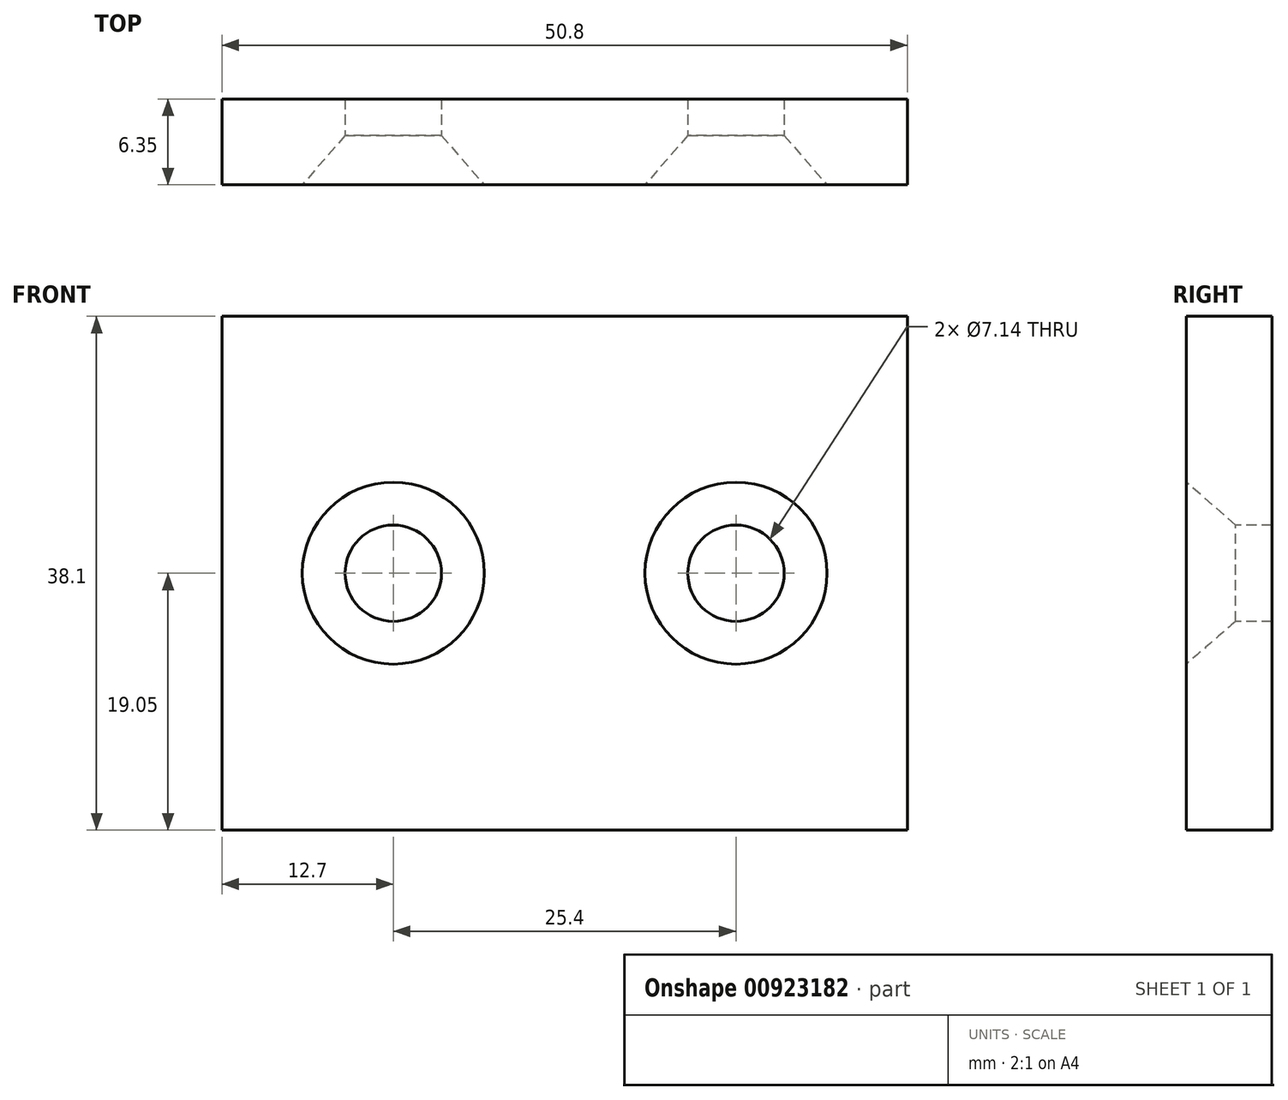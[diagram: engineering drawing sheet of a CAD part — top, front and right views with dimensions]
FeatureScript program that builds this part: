
annotation { "Feature Type Name" : "Feature", "Feature Type Description" : "" }
export const myFeature = defineFeature(function(context is Context, id is Id, definition is map)
    precondition{}
    {
        {
            var Q0;
            Q0=qCreatedBy(makeId("Front.planeOp"),FACE);
            var sketch = newSketch(context, id + "F0", { "sketchPlane" : qUnion([Q0])});
            skLineSegment(sketch, "E0.bottom", {"start": v(0, 0) * mm, "end": v(50.8, 0) * mm});
            skLineSegment(sketch, "E0.top", {"start": v(0, 38.1) * mm, "end": v(50.8, 38.1) * mm});
            skLineSegment(sketch, "E0.left", {"start": v(0, 0) * mm, "end": v(0, 38.1) * mm});
            skLineSegment(sketch, "E0.right", {"start": v(50.8, 0) * mm, "end": v(50.8, 38.1) * mm});
            skSolve(sketch);
        }
        {
            var Q0;
            Q0=makeQuery(id+"F0.imprint","IMPRINT",FACE,{"disambiguationData":[TD([[makeQuery(id+"F0.imprint","IMPRINT",EDGE,{"derivedFrom":sQuery(id+"F0.wireOp",EDGE,"E0.bottom")}),1.0]])]});
            extrude(context, id + "F1", {"entities" : qUnion([Q0]), "depth" : 6.35 * mm, "offsetDistance" : 25.4 * mm});
        }
        {
            var Q0;
            Q0=makeQuery(id+"F1.opExtrude","CAP_FACE",FACE,{"disambiguationData":[OSD([sQuery(id+"F0.wireOp",EDGE,"E0.bottom"),sQuery(id+"F0.wireOp",EDGE,"E0.top"),sQuery(id+"F0.wireOp",EDGE,"E0.left"),sQuery(id+"F0.wireOp",EDGE,"E0.right")])],"isStart":false});
            var sketch = newSketch(context, id + "F2", { "sketchPlane" : qUnion([Q0])});
            skLineSegment(sketch, "E1", {"start": v(50.8, 19.05) * mm, "end": v(38.1, 19.05) * mm});
            skLineSegment(sketch, "E2", {"start": v(0, 19.05) * mm, "end": v(12.7, 19.05) * mm});
            skSolve(sketch);
        }
        {
            var Q0;
            Q0=sQuery(id+"F2.wireOp",VERTEX,"E2.end");
            var Q1;
            Q1=sQuery(id+"F2.wireOp",VERTEX,"E1.end");
            var Q2;
            Q2=makeQuery(id+"F1.opExtrude","SWEPT_BODY",BODY,{"disambiguationData":[OSD([sQuery(id+"F0.wireOp",EDGE,"E0.bottom"),sQuery(id+"F0.wireOp",EDGE,"E0.top"),sQuery(id+"F0.wireOp",EDGE,"E0.left"),sQuery(id+"F0.wireOp",EDGE,"E0.right")])]});
            hole(context, id + "F3", {"style" : HoleStyle.C_SINK, "endStyle" : HoleEndStyle.THROUGH, "standardTappedOrClearance" : lookupTablePath({ "fit" : "Normal (ASME)", "standard" : "ANSI", "size" : "1/4", "type" : "Clearance" }), "standardBlindInLast" : lookupTablePath({ "fit" : "Normal", "standard" : "ANSI", "size" : "1/4", "type" : "Clearance" }), "holeDiameter" : 7.14 * mm, "cSinkDiameter" : 13.5 * mm, "cSinkAngle" : 82 * degree, "majorDiameter" : 6.35 * mm, "isTappedThrough" : true, "tappedDepth" : 12.7 * mm, "tapClearance" : 3, "locations" : qUnion([Q0, Q1]), "scope" : qUnion([Q2])});
        }
    });
